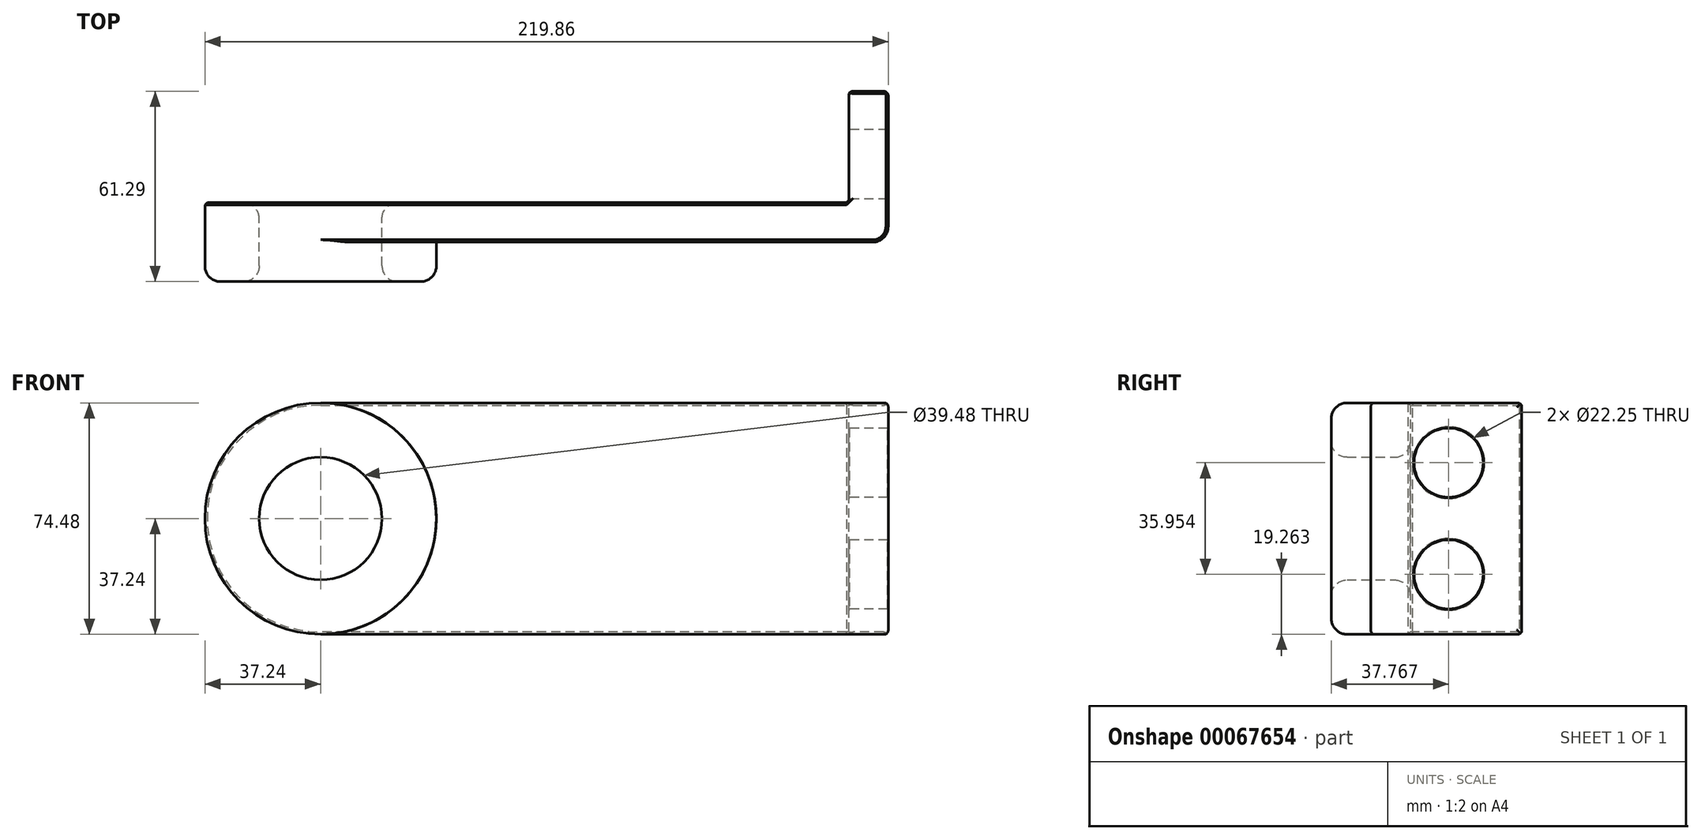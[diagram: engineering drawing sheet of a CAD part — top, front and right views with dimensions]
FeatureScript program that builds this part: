
annotation { "Feature Type Name" : "Feature", "Feature Type Description" : "" }
export const myFeature = defineFeature(function(context is Context, id is Id, definition is map)
    precondition{}
    {
        {
            var Q0;
            Q0=qCreatedBy(makeId("Front.planeOp"),FACE);
            var sketch = newSketch(context, id + "F0", { "sketchPlane" : qUnion([Q0])});
            skLineSegment(sketch, "E0.bottom", {"start": v(0, 0) * mm, "end": v(169.92, 0) * mm});
            skLineSegment(sketch, "E0.top", {"start": v(0, 74.48) * mm, "end": v(169.92, 74.48) * mm});
            skLineSegment(sketch, "E0.left", {"start": v(0, 0) * mm, "end": v(0, 74.48) * mm});
            skLineSegment(sketch, "E0.right", {"start": v(169.92, 0) * mm, "end": v(169.92, 74.48) * mm});
            skCircle(sketch, "E1", {"center": v(0, 37.24) * mm, "radius": 37.24 * mm});
            skCircle(sketch, "E2", {"center": v(0, 37.24) * mm, "radius": 19.74 * mm});
            skSolve(sketch);
        }
        {
            var Q0;
            {var subQ1=sQuery(id+"F0.wireOp",EDGE,"E0.left");var subQ3=sQuery(id+"F0.wireOp",EDGE,"E2");var subQ4=makeQuery(id+"F0.imprint","INTERSECT",VERTEX,{"disambiguationData":[OD(0.0)],"derivedFrom":[subQ1,subQ3]});Q0=makeQuery(id+"F0.imprint","IMPRINT",FACE,{"disambiguationData":[TD([[makeQuery(id+"F0.imprint","IMPRINT",EDGE,{"disambiguationData":[TD([[subQ4,-1.0]])],"derivedFrom":subQ3}),-1.0]])]});}
            var Q1;
            {var subQ1=sQuery(id+"F0.wireOp",EDGE,"E0.left");var subQ3=sQuery(id+"F0.wireOp",EDGE,"E2");var subQ4=makeQuery(id+"F0.imprint","INTERSECT",VERTEX,{"disambiguationData":[OD(0.0)],"derivedFrom":[subQ1,subQ3]});Q1=makeQuery(id+"F0.imprint","IMPRINT",FACE,{"disambiguationData":[TD([[makeQuery(id+"F0.imprint","IMPRINT",EDGE,{"disambiguationData":[TD([[subQ4,1.0]])],"derivedFrom":subQ3}),-1.0]])]});}
            extrude(context, id + "F1", {"entities" : qUnion([Q0, Q1]), "depth" : 25.4 * mm});
        }
        {
            var Q0;
            {var subQ0=sQuery(id+"F0.wireOp",EDGE,"E0.bottom");Q0=makeQuery(id+"F0.imprint","IMPRINT",FACE,{"disambiguationData":[TD([[makeQuery(id+"F0.imprint","IMPRINT",EDGE,{"derivedFrom":subQ0}),1.0]])]});}
            extrude(context, id + "F2", {"entities" : qUnion([Q0]), "operationType" : NewBodyOperationType.ADD, "depth" : 12.7 * mm});
        }
        {
            var Q0;
            Q0=makeQuery(id+"F2.opExtrude","SWEPT_FACE",FACE,{"disambiguationData":[OSD([sQuery(id+"F0.wireOp",EDGE,"E0.right")])]});
            var sketch = newSketch(context, id + "F3", { "sketchPlane" : qUnion([Q0])});
            skPoint(sketch, "E3.oppositeSnap0", {"position": v(-6.35, 0) * mm});
            skLineSegment(sketch, "E3.bottom", {"start": v(-12.7, 74.48) * mm, "end": v(35.89, 74.48) * mm});
            skLineSegment(sketch, "E3.top", {"start": v(-12.7, 0) * mm, "end": v(35.89, 0) * mm});
            skLineSegment(sketch, "E3.left", {"start": v(-12.7, 74.48) * mm, "end": v(-12.7, 0) * mm});
            skLineSegment(sketch, "E3.right", {"start": v(35.89, 74.48) * mm, "end": v(35.89, 0) * mm});
            skLineSegment(sketch, "E4", {"start": v(-12.7, 37.24) * mm, "end": v(35.89, 37.24) * mm, "construction": true});
            skCircle(sketch, "E5", {"center": v(12.37, 19.26) * mm, "radius": 11.13 * mm});
            skCircle(sketch, "E6.MirrorC", {"center": v(12.37, 55.22) * mm, "radius": 11.13 * mm});
            skSolve(sketch);
        }
        {
            var Q0;
            {var subQ2=sQuery(id+"F3.wireOp",EDGE,"E3.right");Q0=makeQuery(id+"F3.imprint","IMPRINT",FACE,{"disambiguationData":[TD([[makeQuery(id+"F3.imprint","IMPRINT",EDGE,{"derivedFrom":subQ2}),-1.0]])]});}
            var Q1;
            {var subQ2=sQuery(id+"F3.wireOp",EDGE,"E3.left");Q1=makeQuery(id+"F3.imprint","IMPRINT",FACE,{"disambiguationData":[TD([[makeQuery(id+"F3.imprint","IMPRINT",EDGE,{"derivedFrom":subQ2}),-1.0]])]});}
            extrude(context, id + "F4", {"entities" : qUnion([Q0, Q1]), "operationType" : NewBodyOperationType.ADD, "depth" : 12.7 * mm});
        }
        {
            var Q0;
            Q0=makeQuery(id+"F1.opExtrude","CAP_EDGE",EDGE,{"disambiguationData":[OSD([sQuery(id+"F0.wireOp",EDGE,"E2")])],"isStart":false});
            var Q1;
            Q1=makeQuery(id+"F4.opExtrude","CAP_EDGE",EDGE,{"disambiguationData":[OSD([sQuery(id+"F3.wireOp",EDGE,"E3.left")])],"isStart":false});
            fillet(context, id + "F5", {"entities" : qUnion([Q0, Q1]), "radius" : 5.08 * mm, "tangentPropagation" : true, "allowEdgeOverflow" : false});
        }
        {
            var Q0;
            Q0=makeQuery(id+"F4.opExtrude","CAP_EDGE",EDGE,{"disambiguationData":[OSD([sQuery(id+"F3.wireOp",EDGE,"E5")])],"isStart":false});
            var Q1;
            Q1=makeQuery(id+"F4.opExtrude","CAP_EDGE",EDGE,{"disambiguationData":[OSD([sQuery(id+"F3.wireOp",EDGE,"E5")])],"isStart":true});
            var Q2;
            Q2=makeQuery(id+"F4.opExtrude","CAP_EDGE",EDGE,{"disambiguationData":[OSD([sQuery(id+"F3.wireOp",EDGE,"E6.MirrorC")])],"isStart":false});
            var Q3;
            Q3=makeQuery(id+"F4.opExtrude","CAP_EDGE",EDGE,{"disambiguationData":[OSD([sQuery(id+"F3.wireOp",EDGE,"E6.MirrorC")])],"isStart":true});
            chamfer(context, id + "F6", {"entities" : qUnion([Q0, Q1, Q2, Q3]), "width" : 0.15 * mm, "tangentPropagation" : true});
        }
        {
            var Q0;
            Q0=makeQuery(id+"F4.opExtrude","CAP_FACE",FACE,{"disambiguationData":[OSD([sQuery(id+"F3.wireOp",EDGE,"E3.bottom"),sQuery(id+"F3.wireOp",EDGE,"E3.top"),sQuery(id+"F3.wireOp",EDGE,"E3.left"),sQuery(id+"F3.wireOp",EDGE,"E3.right"),sQuery(id+"F3.wireOp",EDGE,"E5"),sQuery(id+"F3.wireOp",EDGE,"E6.MirrorC")])],"isStart":true});
            var Q1;
            Q1=makeQuery(id+"F4.boolean.opBoolean","MERGE",FACE,{"derivedFrom":[makeQuery(id+"F2.opExtrude","SWEPT_FACE",FACE,{"disambiguationData":[OSD([sQuery(id+"F0.wireOp",EDGE,"E0.top")])]}),makeQuery(id+"F4.opExtrude","SWEPT_FACE",FACE,{"disambiguationData":[OSD([sQuery(id+"F3.wireOp",EDGE,"E3.bottom")])]})]});
            var Q2;
            Q2=makeQuery(id+"F4.boolean.opBoolean","MERGE",FACE,{"derivedFrom":[makeQuery(id+"F2.opExtrude","SWEPT_FACE",FACE,{"disambiguationData":[OSD([sQuery(id+"F0.wireOp",EDGE,"E0.bottom")])]}),makeQuery(id+"F4.opExtrude","SWEPT_FACE",FACE,{"disambiguationData":[OSD([sQuery(id+"F3.wireOp",EDGE,"E3.top")])]})]});
            chamfer(context, id + "F7", {"entities" : qUnion([Q0, Q1, Q2]), "width" : 0.76 * mm, "tangentPropagation" : true});
        }
        {
            var Q0;
            Q0=makeQuery(id+"F1.opExtrude","SWEPT_FACE",FACE,{"disambiguationData":[OSD([sQuery(id+"F0.wireOp",EDGE,"E2")])]});
            fillet(context, id + "F8", {"entities" : qUnion([Q0]), "radius" : 5.08 * mm, "tangentPropagation" : true, "allowEdgeOverflow" : false});
        }
        {
            var Q0;
            Q0=makeQuery(id+"F2.opExtrude","CAP_EDGE",EDGE,{"disambiguationData":[OSD([sQuery(id+"F0.wireOp",EDGE,"E1")])],"isStart":false});
            var Q1;
            Q1=makeQuery(id+"F1.opExtrude","CAP_EDGE",EDGE,{"disambiguationData":[OSD([sQuery(id+"F0.wireOp",EDGE,"E1")])],"isStart":false});
            fillet(context, id + "F9", {"entities" : qUnion([Q0, Q1]), "radius" : 5.08 * mm, "tangentPropagation" : true, "allowEdgeOverflow" : false});
        }
        {
            var Q0;
            {var subQ0=sQuery(id+"F3.wireOp",EDGE,"E3.bottom");Q0=makeQuery(id+"F7.opChamfer","BLEND_EDGE",EDGE,{"blendedFrom":[makeQuery(id+"F4.opExtrude","CAP_EDGE",EDGE,{"disambiguationData":[OSD([subQ0])],"isStart":false}),makeQuery(id+"F4.opExtrude","CAP_FACE",FACE,{"disambiguationData":[OSD([subQ0,sQuery(id+"F3.wireOp",EDGE,"E3.top"),sQuery(id+"F3.wireOp",EDGE,"E3.left"),sQuery(id+"F3.wireOp",EDGE,"E3.right"),sQuery(id+"F3.wireOp",EDGE,"E5"),sQuery(id+"F3.wireOp",EDGE,"E6.MirrorC")])],"isStart":false})],"blendedInto":[makeQuery(id+"F4.opExtrude","CAP_FACE",FACE,{"disambiguationData":[OSD([subQ0,sQuery(id+"F3.wireOp",EDGE,"E3.top"),sQuery(id+"F3.wireOp",EDGE,"E3.left"),sQuery(id+"F3.wireOp",EDGE,"E3.right"),sQuery(id+"F3.wireOp",EDGE,"E5"),sQuery(id+"F3.wireOp",EDGE,"E6.MirrorC")])],"isStart":false})]});}
            var Q1;
            {var subQ0=sQuery(id+"F3.wireOp",EDGE,"E3.bottom");Q1=makeQuery(id+"F7.opChamfer","BLEND_EDGE",EDGE,{"blendedFrom":[makeQuery(id+"F4.opExtrude","CAP_EDGE",EDGE,{"disambiguationData":[OSD([subQ0])],"isStart":true}),makeQuery(id+"F4.boolean.opBoolean","MERGE",FACE,{"derivedFrom":[makeQuery(id+"F2.opExtrude","SWEPT_FACE",FACE,{"disambiguationData":[OSD([sQuery(id+"F0.wireOp",EDGE,"E0.top")])]}),makeQuery(id+"F4.opExtrude","SWEPT_FACE",FACE,{"disambiguationData":[OSD([subQ0])]})]})],"blendedInto":[makeQuery(id+"F4.boolean.opBoolean","MERGE",FACE,{"derivedFrom":[makeQuery(id+"F2.opExtrude","SWEPT_FACE",FACE,{"disambiguationData":[OSD([sQuery(id+"F0.wireOp",EDGE,"E0.top")])]}),makeQuery(id+"F4.opExtrude","SWEPT_FACE",FACE,{"disambiguationData":[OSD([subQ0])]})]})]});}
            var Q2;
            {var subQ0=sQuery(id+"F3.wireOp",EDGE,"E3.right");Q2=makeQuery(id+"F7.opChamfer","BLEND_EDGE",EDGE,{"blendedFrom":[makeQuery(id+"F4.opExtrude","CAP_EDGE",EDGE,{"disambiguationData":[OSD([subQ0])],"isStart":true}),makeQuery(id+"F4.opExtrude","SWEPT_FACE",FACE,{"disambiguationData":[OSD([subQ0])]})],"blendedInto":[makeQuery(id+"F4.opExtrude","SWEPT_FACE",FACE,{"disambiguationData":[OSD([subQ0])]})]});}
            var Q3;
            Q3=makeQuery(id+"F4.opExtrude","CAP_EDGE",EDGE,{"disambiguationData":[OSD([sQuery(id+"F3.wireOp",EDGE,"E3.right")])],"isStart":false});
            var Q4;
            {var subQ0=sQuery(id+"F3.wireOp",EDGE,"E3.top");Q4=makeQuery(id+"F7.opChamfer","BLEND_EDGE",EDGE,{"blendedFrom":[makeQuery(id+"F4.opExtrude","CAP_EDGE",EDGE,{"disambiguationData":[OSD([subQ0])],"isStart":true}),makeQuery(id+"F4.boolean.opBoolean","MERGE",FACE,{"derivedFrom":[makeQuery(id+"F2.opExtrude","SWEPT_FACE",FACE,{"disambiguationData":[OSD([sQuery(id+"F0.wireOp",EDGE,"E0.bottom")])]}),makeQuery(id+"F4.opExtrude","SWEPT_FACE",FACE,{"disambiguationData":[OSD([subQ0])]})]})],"blendedInto":[makeQuery(id+"F4.boolean.opBoolean","MERGE",FACE,{"derivedFrom":[makeQuery(id+"F2.opExtrude","SWEPT_FACE",FACE,{"disambiguationData":[OSD([sQuery(id+"F0.wireOp",EDGE,"E0.bottom")])]}),makeQuery(id+"F4.opExtrude","SWEPT_FACE",FACE,{"disambiguationData":[OSD([subQ0])]})]})]});}
            var Q5;
            {var subQ0=sQuery(id+"F3.wireOp",EDGE,"E3.top");Q5=makeQuery(id+"F7.opChamfer","BLEND_EDGE",EDGE,{"blendedFrom":[makeQuery(id+"F4.opExtrude","CAP_EDGE",EDGE,{"disambiguationData":[OSD([subQ0])],"isStart":false}),makeQuery(id+"F4.opExtrude","CAP_FACE",FACE,{"disambiguationData":[OSD([sQuery(id+"F3.wireOp",EDGE,"E3.bottom"),subQ0,sQuery(id+"F3.wireOp",EDGE,"E3.left"),sQuery(id+"F3.wireOp",EDGE,"E3.right"),sQuery(id+"F3.wireOp",EDGE,"E5"),sQuery(id+"F3.wireOp",EDGE,"E6.MirrorC")])],"isStart":false})],"blendedInto":[makeQuery(id+"F4.opExtrude","CAP_FACE",FACE,{"disambiguationData":[OSD([sQuery(id+"F3.wireOp",EDGE,"E3.bottom"),subQ0,sQuery(id+"F3.wireOp",EDGE,"E3.left"),sQuery(id+"F3.wireOp",EDGE,"E3.right"),sQuery(id+"F3.wireOp",EDGE,"E5"),sQuery(id+"F3.wireOp",EDGE,"E6.MirrorC")])],"isStart":false})]});}
            fillet(context, id + "F10", {"entities" : qUnion([Q0, Q1, Q2, Q3, Q4, Q5]), "radius" : 1.52 * mm, "tangentPropagation" : true, "allowEdgeOverflow" : false});
        }
    });
